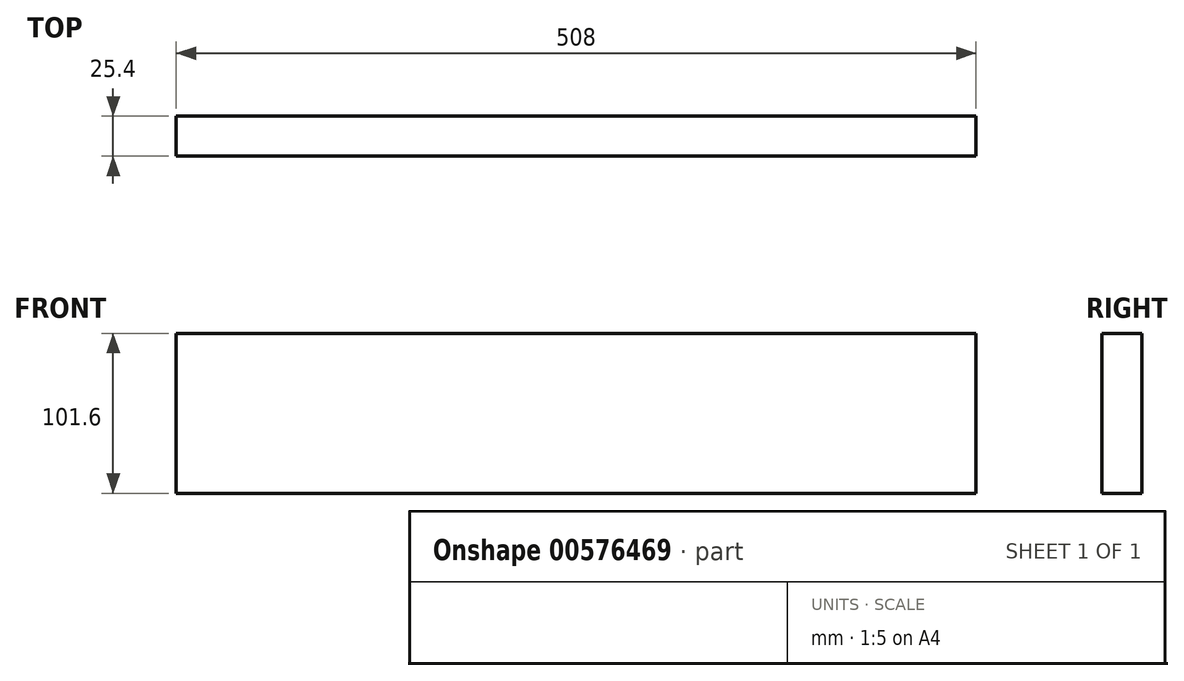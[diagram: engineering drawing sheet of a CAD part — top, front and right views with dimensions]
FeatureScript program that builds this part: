
annotation { "Feature Type Name" : "Feature", "Feature Type Description" : "" }
export const myFeature = defineFeature(function(context is Context, id is Id, definition is map)
    precondition{}
    {
        {
            var Q0;
            Q0=qCreatedBy(makeId("Front.planeOp"),FACE);
            var sketch = newSketch(context, id + "F0", { "sketchPlane" : qUnion([Q0])});
            skLineSegment(sketch, "E0.bottom", {"start": v(0, 0) * mm, "end": v(508, 0) * mm});
            skLineSegment(sketch, "E0.top", {"start": v(0, 101.6) * mm, "end": v(508, 101.6) * mm});
            skLineSegment(sketch, "E0.left", {"start": v(0, 0) * mm, "end": v(0, 101.6) * mm});
            skLineSegment(sketch, "E0.right", {"start": v(508, 0) * mm, "end": v(508, 101.6) * mm});
            skSolve(sketch);
        }
        {
            var Q0;
            Q0=makeQuery(id+"F0.imprint","IMPRINT",FACE,{"disambiguationData":[TD([[makeQuery(id+"F0.imprint","IMPRINT",EDGE,{"derivedFrom":sQuery(id+"F0.wireOp",EDGE,"E0.bottom")}),1.0]])]});
            extrude(context, id + "F1", {"entities" : qUnion([Q0]), "depth" : 25.4 * mm, "offsetDistance" : 25.4 * mm});
        }
        {
            var Q0;
            Q0=makeQuery(id+"F1.opExtrude","SWEPT_FACE",FACE,{"disambiguationData":[OSD([sQuery(id+"F0.wireOp",EDGE,"E0.right")])]});
            var sketch = newSketch(context, id + "F2", { "sketchPlane" : qUnion([Q0])});
            skLineSegment(sketch, "E1", {"start": v(0, 101.6) * mm, "end": v(-25.4, 0) * mm});
            skSolve(sketch);
        }
        {
            var Q0;
            Q0=makeQuery(id+"F2.imprint","IMPRINT",FACE,{"disambiguationData":[TD([[makeQuery(id+"F2.imprint","IMPRINT",EDGE,{"derivedFrom":sQuery(id+"F2.wireOp",EDGE,"E1")}),-1.0]])]});
            extrude(context, id + "F3", {"entities" : qUnion([Q0]), "operationType" : NewBodyOperationType.REMOVE, "depth" : 25.4 * mm, "offsetDistance" : 25.4 * mm});
        }
    });
